# Revit family: ЭВАН NEXT PLUS 3-28 кВт
name_source: partatom
category: Оборудование
units: mm (PartAtom-declared; Revit-internal decimal feet)

## family parameters
Всегда вертикально = Да
Классификация = Нет
На основе рабочей плоскости = Да
Общий = Нет
При загрузке вырезать с полостями = Нет
Размер круглого соединителя = Использовать диаметр
Тип детали = Нормальный
Точка расчета площади = Нет

## types (16) — shared parameters
ADSK_Классификация нагрузок = Прочее
ADSK_Материал = Сталь
ADSK_Размер_Высота = 670 мм
ADSK_Размер_Длина = 330 мм
ADSK_Размер_Ширина = 200 мм
ADSK_Расход теплоносителя = 0.0 м³/ч
Dn = 20 мм
База = ЭЛЕКТРИЧЕСКИЙ ТЕПЛОГЕНЕРАТОР (КОТЕЛ)
Диапазон регулируемых температур теплоносителя, оС = От +10 до +85
Максимальная температура теплоносителя, оС = +85
Материал корпуса = Сталь
Минимальная температура теплоносителя, оС = +10
Объем колбы котла, л = 8.3
Рабочее давление, МПа = 0.07-0.3
Резьба патрубков для подключения трубопроводов теплоносителя = G3/4
zero-valued in all types: Отметка по умолчанию

## per-type parameters (varying)
| type | ADSK_Количество фаз | ADSK_Номинальная мощность | Потребляемая электрическая мощность при максимальной тепловой мощность  в час, кВт/ч |
| ЭВАН NEXT PLUS 3 кВт 380В | 3 | 3000 Вт | 3.2 |
| ЭВАН NEXT PLUS 3 кВт 220В | 1 | 3000 Вт | 3.2 |
| ЭВАН NEXT PLUS 5 кВт 220В | 1 | 5000 Вт | 5.2 |
| ЭВАН NEXT PLUS 5 кВт 380В | 3 | 5000 Вт | 5.2 |
| ЭВАН NEXT PLUS 6 кВт 380В | 3 | 6000 Вт | 6.3 |
| ЭВАН NEXT PLUS 6 кВт 220В | 1 | 6000 Вт | 6.3 |
| ЭВАН NEXT PLUS 7 кВт 220В | 1 | 7000 Вт | 7.3 |
| ЭВАН NEXT PLUS 7 кВт 380В | 3 | 7000 Вт | 7.3 |
| ЭВАН NEXT PLUS 9 кВт 380В | 3 | 9000 Вт | 9.3 |
| ЭВАН NEXT PLUS 12 кВт | 3 | 12000 Вт | 12.6 |
| ЭВАН NEXT PLUS 14 кВт | 3 | 14000 Вт | 14.7 |
| ЭВАН NEXT PLUS 18 кВт | 3 | 18000 Вт | 18.9 |
| ЭВАН NEXT PLUS 21 кВт | 3 | 21000 Вт | 22.1 |
| ЭВАН NEXT PLUS 24 кВт | 3 | 24000 Вт | 25.2 |
| ЭВАН NEXT PLUS 28 кВт | 3 | 28000 Вт | 29.4 |
| ЭВАН NEXT PLUS 9 кВт 220В | 1 | 9000 Вт | 9.3 |
